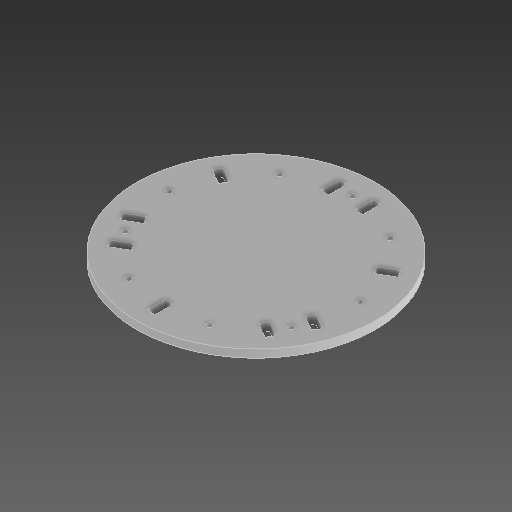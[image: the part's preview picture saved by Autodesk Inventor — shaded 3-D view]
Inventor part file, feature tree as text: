
AUTODESK INVENTOR PART (.ipt)
format: ipt  version: 2020.1 (Build 241239000, 239)  size: 199,168 bytes
history: native  units: mm
features: other x5, extrude x3, pattern_circular x2, hole x2, sketch x1
ambient origin geometry x8: Origin, YZ Plane, XZ Plane, XY Plane, X Axis, Y Axis, Z Axis, Center Point
bodies: Solid1 (feature_tree)
feature tree (13):
  extrude  "Make Prototype Plate Base by Extrusion"  Depth=9.0mm
  extrude  "Cut Outer Rib Slots"  TaperAngle=0.0deg  [1 undecoded]
  pattern_circular  "Pattern Outer Rib Slots Around the Base Plate"  Count=3  [1 undecoded]
  extrude  "Cut Inner Rib Slots"  Depth=20.0mm
  pattern_circular  "Pattern Inner Rib Slots Around the Base Plate"  [2 undecoded]
  hole  "Clearance Holes to Bolt the Two Bases Together"  [1 undecoded]
  hole  "Clearance Holes to Bolt the Two Bases Together at Arms"  [1 undecoded]
  sketch  "Sketch the Prototype Plate Base Profile"  dims[d0=274.0mm d1=9.0mm d2=0.0mm d3=30.0mm d5=20.0mm d15=9.0mm d17=122.0mm d18=9.0mm d19=0.0mm d20=30.0mm d21=360.0deg d27=9.0mm d28=20.0mm d29=220.0mm d30=15.0mm d31=220.0mm d32=60.0deg d33=9.0mm d34=0.0mm d35=30.0mm d36=360.0deg d54=220.0mm d64=30.0mm d66=360.0deg d68=6.4mm d69=6.0mm d70=10.4mm d71=2.0mm d72=90.0deg d73=8.0mm d74=20.594885mm d75=220.0mm d76=30.0mm d78=360.0deg d80=6.4mm d81=6.0mm d82=10.0mm d83=5.7mm d84=90.0deg d85=8.0mm d86=20.594885mm]
  other  "Locate the Outer Rib Slots"
  other  "Projected Base Boundary"
  other  "Locate the Inner Rib Slot"
  other  "Locate Holes for Connecting Two Bases"
  other  "Locate Three More Holes to Support the Connection Between Two Plates Between Outer Ribs"
note: 6 required parameter values undecoded (feature->parameter linkage not recoverable at this tier; creation-order binding heuristic only, values carry confidence <= 0.55)
